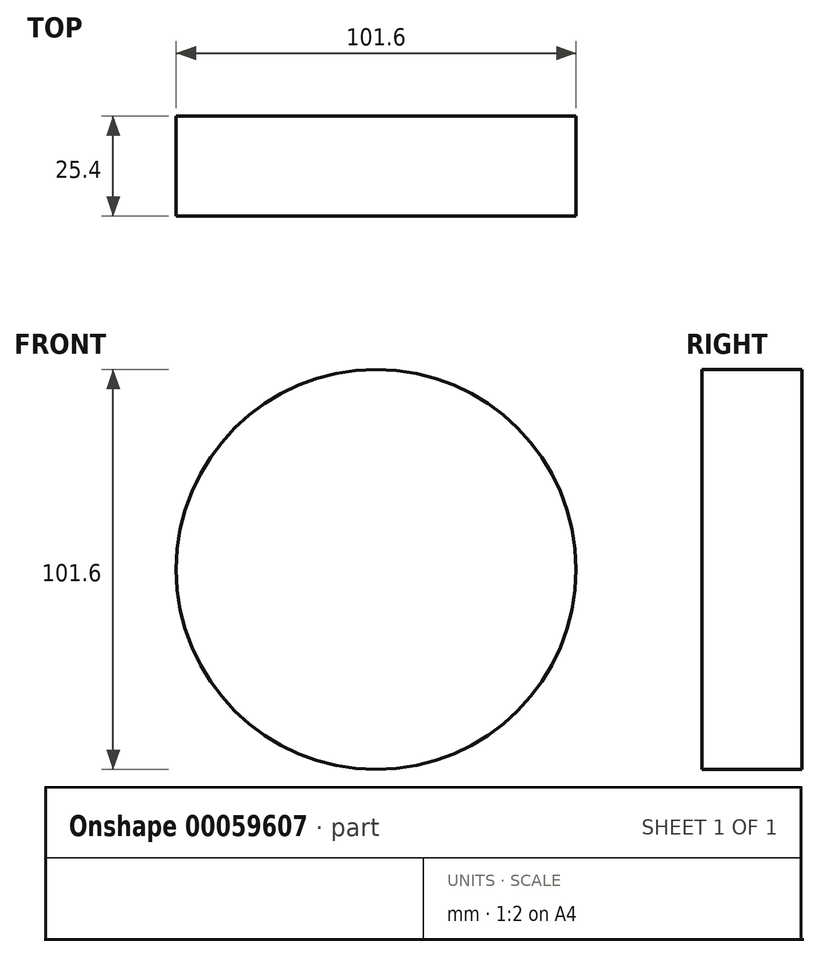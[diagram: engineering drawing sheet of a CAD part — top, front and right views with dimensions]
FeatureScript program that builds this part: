
annotation { "Feature Type Name" : "Feature", "Feature Type Description" : "" }
export const myFeature = defineFeature(function(context is Context, id is Id, definition is map)
    precondition{}
    {
        {
            var Q0;
            Q0=qCreatedBy(makeId("Front.planeOp"),FACE);
            var sketch = newSketch(context, id + "F0", { "sketchPlane" : qUnion([Q0])});
            skCircle(sketch, "E0", {"center": v(0, 0) * mm, "radius": 50.8 * mm});
            skSolve(sketch);
        }
        {
            var Q0;
            Q0 = qConstructionFilter(qBodyType(qCreatedBy(id + "F0" ,EDGE), BodyType.WIRE), ConstructionObject.NO);
            extrude(context, id + "F1", {"bodyType" : ToolBodyType.SURFACE, "surfaceEntities" : qUnion([Q0]), "depth" : 25.4 * mm});
        }
    });
